annotation { "Feature Type Name" : "Feature", "Feature Type Description" : "" }
export const myFeature = defineFeature(function(context is Context, id is Id, definition is map)
    precondition{}
    {
        {
            var Q0;
            Q0=qCreatedBy(makeId("Top.planeOp"),FACE);
            var sketch = newSketch(context, id + "F0", { "sketchPlane" : qUnion([Q0])});
            skArc(sketch, "E0", {"start": v(12, 0) * mm, "mid": v(0, 12) * mm, "end": v(-12, 0) * mm});
            skLineSegment(sketch, "E1", {"start": v(12, 0) * mm, "end": v(12, -20) * mm});
            skLineSegment(sketch, "E2", {"start": v(7, -25) * mm, "end": v(-7, -25) * mm});
            skLineSegment(sketch, "E3", {"start": v(-12, -20) * mm, "end": v(-12, 0) * mm});
            skPoint(sketch, "E4.visualSharp", {"position": v(-12, -25) * mm});
            skArc(sketch, "E4.filletArc", {"start": v(-12, -20) * mm, "mid": v(-10.54, -23.54) * mm, "end": v(-7, -25) * mm});
            skPoint(sketch, "E5.visualSharp", {"position": v(12, -25) * mm});
            skArc(sketch, "E5.filletArc", {"start": v(7, -25) * mm, "mid": v(10.54, -23.54) * mm, "end": v(12, -20) * mm});
            skText(sketch, "E6", { "text": "MZL TV\n YNCH", "fontName": "OpenSans-Bold.ttf"});
            skLineSegment(sketch, "E7", {"start": v(-12, 0) * mm, "end": v(12, 0) * mm, "construction": true});
            const initialGuessF0  = {"E6": [-0.00897, -0.00362, 1, 0, 0.00362]};
            skSetInitialGuess(sketch, initialGuessF0);
            skSolve(sketch);
        }
        {
            var Q0;
            Q0=makeQuery(id+"F0.imprint","IMPRINT",FACE,{"disambiguationData":[TD([[makeQuery(id+"F0.imprint","IMPRINT",EDGE,{"derivedFrom":sQuery(id+"F0.wireOp",EDGE,"E0")}),1.0]])]});
            extrude(context, id + "F1", {"entities" : qUnion([Q0]), "depth" : 2.4 * mm});
        }
        {
            var Q0;
            Q0=makeQuery(id+"F1.opExtrude","CAP_FACE",FACE,{"disambiguationData":[OSD([sQuery(id+"F0.wireOp",EDGE,"E0"),sQuery(id+"F0.wireOp",EDGE,"E1"),sQuery(id+"F0.wireOp",EDGE,"E2"),sQuery(id+"F0.wireOp",EDGE,"E3"),sQuery(id+"F0.wireOp",EDGE,"E4.filletArc"),sQuery(id+"F0.wireOp",EDGE,"E5.filletArc"),sQuery(id+"F0.wireOp",EDGE,"E6.sketch_text.stroke-0"),sQuery(id+"F0.wireOp",EDGE,"E6.sketch_text.stroke-1"),sQuery(id+"F0.wireOp",EDGE,"E6.sketch_text.stroke-2"),sQuery(id+"F0.wireOp",EDGE,"E6.sketch_text.stroke-3"),sQuery(id+"F0.wireOp",EDGE,"E6.sketch_text.stroke-4"),sQuery(id+"F0.wireOp",EDGE,"E6.sketch_text.stroke-5"),sQuery(id+"F0.wireOp",EDGE,"E6.sketch_text.stroke-6"),sQuery(id+"F0.wireOp",EDGE,"E6.sketch_text.stroke-7"),sQuery(id+"F0.wireOp",EDGE,"E6.sketch_text.stroke-8"),sQuery(id+"F0.wireOp",EDGE,"E6.sketch_text.stroke-9"),sQuery(id+"F0.wireOp",EDGE,"E6.sketch_text.stroke-10"),sQuery(id+"F0.wireOp",EDGE,"E6.sketch_text.stroke-11"),sQuery(id+"F0.wireOp",EDGE,"E6.sketch_text.stroke-12"),sQuery(id+"F0.wireOp",EDGE,"E6.sketch_text.stroke-13"),sQuery(id+"F0.wireOp",EDGE,"E6.sketch_text.stroke-14"),sQuery(id+"F0.wireOp",EDGE,"E6.sketch_text.stroke-15"),sQuery(id+"F0.wireOp",EDGE,"E6.sketch_text.stroke-16"),sQuery(id+"F0.wireOp",EDGE,"E6.sketch_text.stroke-17"),sQuery(id+"F0.wireOp",EDGE,"E6.sketch_text.stroke-18"),sQuery(id+"F0.wireOp",EDGE,"E6.sketch_text.stroke-19"),sQuery(id+"F0.wireOp",EDGE,"E6.sketch_text.stroke-20"),sQuery(id+"F0.wireOp",EDGE,"E6.sketch_text.stroke-21"),sQuery(id+"F0.wireOp",EDGE,"E6.sketch_text.stroke-22"),sQuery(id+"F0.wireOp",EDGE,"E6.sketch_text.stroke-23"),sQuery(id+"F0.wireOp",EDGE,"E6.sketch_text.stroke-24"),sQuery(id+"F0.wireOp",EDGE,"E6.sketch_text.stroke-25"),sQuery(id+"F0.wireOp",EDGE,"E6.sketch_text.stroke-26"),sQuery(id+"F0.wireOp",EDGE,"E6.sketch_text.stroke-27"),sQuery(id+"F0.wireOp",EDGE,"E6.sketch_text.stroke-28"),sQuery(id+"F0.wireOp",EDGE,"E6.sketch_text.stroke-29"),sQuery(id+"F0.wireOp",EDGE,"E6.sketch_text.stroke-30"),sQuery(id+"F0.wireOp",EDGE,"E6.sketch_text.stroke-31"),sQuery(id+"F0.wireOp",EDGE,"E6.sketch_text.stroke-32"),sQuery(id+"F0.wireOp",EDGE,"E6.sketch_text.stroke-33"),sQuery(id+"F0.wireOp",EDGE,"E6.sketch_text.stroke-34"),sQuery(id+"F0.wireOp",EDGE,"E6.sketch_text.stroke-35"),sQuery(id+"F0.wireOp",EDGE,"E6.sketch_text.stroke-36"),sQuery(id+"F0.wireOp",EDGE,"E6.sketch_text.stroke-37"),sQuery(id+"F0.wireOp",EDGE,"E6.sketch_text.stroke-38"),sQuery(id+"F0.wireOp",EDGE,"E6.sketch_text.stroke-39"),sQuery(id+"F0.wireOp",EDGE,"E6.sketch_text.stroke-40"),sQuery(id+"F0.wireOp",EDGE,"E6.sketch_text.stroke-41"),sQuery(id+"F0.wireOp",EDGE,"E6.sketch_text.stroke-42"),sQuery(id+"F0.wireOp",EDGE,"E6.sketch_text.stroke-43"),sQuery(id+"F0.wireOp",EDGE,"E6.sketch_text.stroke-44"),sQuery(id+"F0.wireOp",EDGE,"E6.sketch_text.stroke-45"),sQuery(id+"F0.wireOp",EDGE,"E6.sketch_text.stroke-46"),sQuery(id+"F0.wireOp",EDGE,"E6.sketch_text.stroke-47"),sQuery(id+"F0.wireOp",EDGE,"E6.sketch_text.stroke-48"),sQuery(id+"F0.wireOp",EDGE,"E6.sketch_text.stroke-49"),sQuery(id+"F0.wireOp",EDGE,"E6.sketch_text.stroke-50"),sQuery(id+"F0.wireOp",EDGE,"E6.sketch_text.stroke-51"),sQuery(id+"F0.wireOp",EDGE,"E6.sketch_text.stroke-52"),sQuery(id+"F0.wireOp",EDGE,"E6.sketch_text.stroke-53"),sQuery(id+"F0.wireOp",EDGE,"E6.sketch_text.stroke-54"),sQuery(id+"F0.wireOp",EDGE,"E6.sketch_text.stroke-55"),sQuery(id+"F0.wireOp",EDGE,"E6.sketch_text.stroke-56"),sQuery(id+"F0.wireOp",EDGE,"E6.sketch_text.stroke-57"),sQuery(id+"F0.wireOp",EDGE,"E6.sketch_text.stroke-58"),sQuery(id+"F0.wireOp",EDGE,"E6.sketch_text.stroke-59"),sQuery(id+"F0.wireOp",EDGE,"E6.sketch_text.stroke-60"),sQuery(id+"F0.wireOp",EDGE,"E6.sketch_text.stroke-61"),sQuery(id+"F0.wireOp",EDGE,"E6.sketch_text.stroke-62"),sQuery(id+"F0.wireOp",EDGE,"E6.sketch_text.stroke-63"),sQuery(id+"F0.wireOp",EDGE,"E6.sketch_text.stroke-64"),sQuery(id+"F0.wireOp",EDGE,"E6.sketch_text.stroke-65"),sQuery(id+"F0.wireOp",EDGE,"E6.sketch_text.stroke-66"),sQuery(id+"F0.wireOp",EDGE,"E6.sketch_text.stroke-67"),sQuery(id+"F0.wireOp",EDGE,"E6.sketch_text.stroke-68"),sQuery(id+"F0.wireOp",EDGE,"E6.sketch_text.stroke-69"),sQuery(id+"F0.wireOp",EDGE,"E6.sketch_text.stroke-70"),sQuery(id+"F0.wireOp",EDGE,"E6.sketch_text.stroke-71"),sQuery(id+"F0.wireOp",EDGE,"E6.sketch_text.stroke-72"),sQuery(id+"F0.wireOp",EDGE,"E6.sketch_text.stroke-73"),sQuery(id+"F0.wireOp",EDGE,"E6.sketch_text.stroke-74"),sQuery(id+"F0.wireOp",EDGE,"E6.sketch_text.stroke-75"),sQuery(id+"F0.wireOp",EDGE,"E6.sketch_text.stroke-76"),sQuery(id+"F0.wireOp",EDGE,"E6.sketch_text.stroke-77"),sQuery(id+"F0.wireOp",EDGE,"E6.sketch_text.stroke-78"),sQuery(id+"F0.wireOp",EDGE,"E6.sketch_text.stroke-79"),sQuery(id+"F0.wireOp",EDGE,"E6.sketch_text.stroke-80"),sQuery(id+"F0.wireOp",EDGE,"E6.sketch_text.stroke-81"),sQuery(id+"F0.wireOp",EDGE,"E6.sketch_text.stroke-82"),sQuery(id+"F0.wireOp",EDGE,"E6.sketch_text.stroke-83"),sQuery(id+"F0.wireOp",EDGE,"E6.sketch_text.stroke-84"),sQuery(id+"F0.wireOp",EDGE,"E6.sketch_text.stroke-85"),sQuery(id+"F0.wireOp",EDGE,"E6.sketch_text.stroke-86"),sQuery(id+"F0.wireOp",EDGE,"E6.sketch_text.stroke-87"),sQuery(id+"F0.wireOp",EDGE,"E6.sketch_text.stroke-88"),sQuery(id+"F0.wireOp",EDGE,"E6.sketch_text.stroke-89"),sQuery(id+"F0.wireOp",EDGE,"E6.sketch_text.stroke-90"),sQuery(id+"F0.wireOp",EDGE,"E6.sketch_text.stroke-91"),sQuery(id+"F0.wireOp",EDGE,"E6.sketch_text.stroke-92"),sQuery(id+"F0.wireOp",EDGE,"E6.sketch_text.stroke-93"),sQuery(id+"F0.wireOp",EDGE,"E6.sketch_text.stroke-94"),sQuery(id+"F0.wireOp",EDGE,"E6.sketch_text.stroke-95"),sQuery(id+"F0.wireOp",EDGE,"E6.sketch_text.stroke-96"),sQuery(id+"F0.wireOp",EDGE,"E6.sketch_text.stroke-97"),sQuery(id+"F0.wireOp",EDGE,"E6.sketch_text.stroke-98"),sQuery(id+"F0.wireOp",EDGE,"E6.sketch_text.stroke-99"),sQuery(id+"F0.wireOp",EDGE,"E6.sketch_text.stroke-100"),sQuery(id+"F0.wireOp",EDGE,"E6.sketch_text.stroke-101"),sQuery(id+"F0.wireOp",EDGE,"E6.sketch_text.stroke-102")])],"isStart":false});
            var sketch = newSketch(context, id + "F2", { "sketchPlane" : qUnion([Q0])});
            skLineSegment(sketch, "E8", {"start": v(-12, -14.9) * mm, "end": v(12, -14.9) * mm, "construction": true});
            skLineSegment(sketch, "E9", {"start": v(12, -14.9) * mm, "end": v(0, -14.9) * mm});
            skLineSegment(sketch, "E10", {"start": v(0, -14.9) * mm, "end": v(0, -25) * mm, "construction": true});
            skSolve(sketch);
        }
        {
            var Q0;
            {var subQ2=makeQuery(id+"F1.opExtrude","CAP_EDGE",EDGE,{"disambiguationData":[OSD([sQuery(id+"F0.wireOp",EDGE,"E0")])],"isStart":false});Q0=makeQuery(id+"F2.imprint","IMPRINT",FACE,{"disambiguationData":[TD([[makeQuery(id+"F2.imprint","IMPRINT",EDGE,{"derivedFrom":subQ2}),1.0]])]});}
            var sketch = newSketch(context, id + "F3", { "sketchPlane" : qUnion([Q0])});
            skText(sketch, "E11", { "text": "28/10/15\n", "fontName": "OpenSans-Regular.ttf"});
            const initialGuessF3  = {"E11": [-0.0075, -0.0185, 1, 0, 0.00263]};
            skSetInitialGuess(sketch, initialGuessF3);
            skSolve(sketch);
        }
        {
            var Q0;
            Q0 = qSketchRegion(id + "F3", true);
            extrude(context, id + "F4", {"entities" : qUnion([Q0]), "operationType" : NewBodyOperationType.REMOVE, "oppositeDirection" : true, "depth" : 25 * mm});
        }
        {
            var Q0;
            {var subQ2=makeQuery(id+"F1.opExtrude","CAP_EDGE",EDGE,{"disambiguationData":[OSD([sQuery(id+"F0.wireOp",EDGE,"E0")])],"isStart":false});Q0=makeQuery(id+"F2.imprint","IMPRINT",FACE,{"disambiguationData":[TD([[makeQuery(id+"F2.imprint","IMPRINT",EDGE,{"derivedFrom":subQ2}),1.0]])]});}
            var sketch = newSketch(context, id + "F5", { "sketchPlane" : qUnion([Q0])});
            skLineSegment(sketch, "E12.rect.bottom", {"start": v(4.4, -20.2) * mm, "end": v(-2.4, -20.2) * mm});
            skLineSegment(sketch, "E12.rect.top", {"start": v(2.4, -23) * mm, "end": v(-4.4, -23) * mm});
            skLineSegment(sketch, "E12.rect.left", {"start": v(4.4, -20.2) * mm, "end": v(4.4, -21) * mm});
            skLineSegment(sketch, "E12.rect.right", {"start": v(-4.4, -22.2) * mm, "end": v(-4.4, -23) * mm});
            skPoint(sketch, "E12.rect.middle", {"position": v(0, -21.6) * mm});
            skPoint(sketch, "E13.visualSharp", {"position": v(-4.4, -20.2) * mm});
            skArc(sketch, "E13.filletArc", {"start": v(-2.4, -20.2) * mm, "mid": v(-3.81, -20.8) * mm, "end": v(-4.4, -22.2) * mm});
            skPoint(sketch, "E14.visualSharp", {"position": v(4.4, -23) * mm});
            skArc(sketch, "E14.filletArc", {"start": v(2.4, -23) * mm, "mid": v(3.81, -22.41) * mm, "end": v(4.4, -21) * mm});
            skSolve(sketch);
        }
        {
            var Q0;
            Q0 = qSketchRegion(id + "F5", true);
            extrude(context, id + "F6", {"entities" : qUnion([Q0]), "operationType" : NewBodyOperationType.REMOVE, "oppositeDirection" : true, "depth" : 25 * mm});
        }
    });